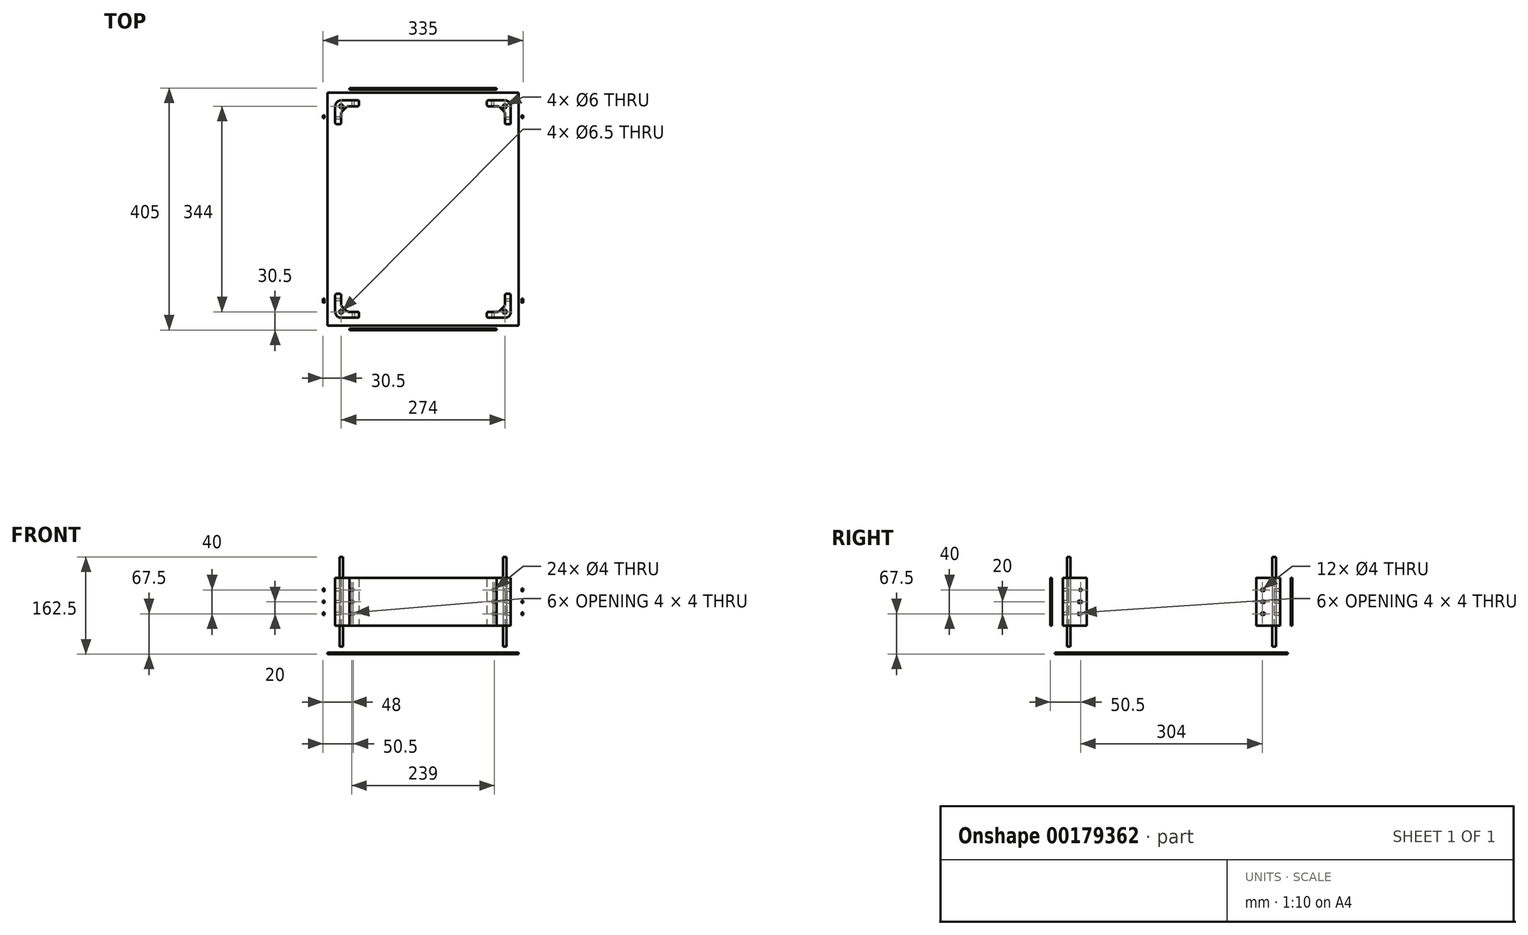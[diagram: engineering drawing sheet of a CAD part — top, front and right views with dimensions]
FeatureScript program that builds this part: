
annotation { "Feature Type Name" : "Feature", "Feature Type Description" : "" }
export const myFeature = defineFeature(function(context is Context, id is Id, definition is map)
    precondition{}
    {
        {
            var Q0;
            Q0=qCreatedBy(makeId("Top.planeOp"),FACE);
            var sketch = newSketch(context, id + "F0", { "sketchPlane" : qUnion([Q0])});
            skLineSegment(sketch, "E0.bottom", {"start": v(140, -175) * mm, "end": v(-140, -175) * mm, "construction": true});
            skLineSegment(sketch, "E0.top", {"start": v(140, 175) * mm, "end": v(-140, 175) * mm, "construction": true});
            skLineSegment(sketch, "E0.left", {"start": v(140, -175) * mm, "end": v(140, 175) * mm, "construction": true});
            skLineSegment(sketch, "E0.right", {"start": v(-140, -175) * mm, "end": v(-140, 175) * mm, "construction": true});
            skLineSegment(sketch, "E1", {"start": v(-134, 175) * mm, "end": v(-134, -175) * mm, "construction": true});
            skLineSegment(sketch, "E2", {"start": v(-140, -169) * mm, "end": v(140, -169) * mm, "construction": true});
            skLineSegment(sketch, "E3", {"start": v(134, -175) * mm, "end": v(134, 175) * mm, "construction": true});
            skLineSegment(sketch, "E4", {"start": v(-140, 169) * mm, "end": v(140, 169) * mm, "construction": true});
            skPoint(sketch, "E5", {"position": v(-134, -169) * mm});
            skPoint(sketch, "E6", {"position": v(134, -169) * mm});
            skPoint(sketch, "E7", {"position": v(134, 169) * mm});
            skPoint(sketch, "E8", {"position": v(-134, 169) * mm});
            skLineSegment(sketch, "E9", {"start": v(-140, 175) * mm, "end": v(-134, 169) * mm, "construction": true});
            skLineSegment(sketch, "E10", {"start": v(-134, 175) * mm, "end": v(-140, 169) * mm, "construction": true});
            skPoint(sketch, "E11", {"position": v(-137, 172) * mm});
            skCircle(sketch, "E12", {"center": v(-137, 172) * mm, "radius": 3 * mm});
            skLineSegment(sketch, "E13", {"start": v(134, 169) * mm, "end": v(140, 175) * mm, "construction": true});
            skLineSegment(sketch, "E14", {"start": v(134, 175) * mm, "end": v(140, 169) * mm, "construction": true});
            skPoint(sketch, "E15", {"position": v(137, 172) * mm});
            skCircle(sketch, "E16", {"center": v(137, 172) * mm, "radius": 3 * mm});
            skLineSegment(sketch, "E17", {"start": v(134, -169) * mm, "end": v(140, -175) * mm, "construction": true});
            skLineSegment(sketch, "E18", {"start": v(140, -169) * mm, "end": v(134, -175) * mm, "construction": true});
            skPoint(sketch, "E19", {"position": v(137, -172) * mm});
            skCircle(sketch, "E20", {"center": v(137, -172) * mm, "radius": 3 * mm});
            skLineSegment(sketch, "E21", {"start": v(-134, -169) * mm, "end": v(-140, -175) * mm, "construction": true});
            skLineSegment(sketch, "E22", {"start": v(-140, -169) * mm, "end": v(-134, -175) * mm, "construction": true});
            skPoint(sketch, "E23", {"position": v(-137, -172) * mm});
            skCircle(sketch, "E24", {"center": v(-137, -172) * mm, "radius": 3 * mm});
            skLineSegment(sketch, "E25.bottom", {"start": v(160, -195) * mm, "end": v(-160, -195) * mm});
            skLineSegment(sketch, "E25.top", {"start": v(160, 195) * mm, "end": v(-160, 195) * mm});
            skLineSegment(sketch, "E25.left", {"start": v(160, -195) * mm, "end": v(160, 195) * mm});
            skLineSegment(sketch, "E25.right", {"start": v(-160, -195) * mm, "end": v(-160, 195) * mm});
            skPoint(sketch, "E25.middle", {"position": v(0, 0) * mm});
            skSolve(sketch);
        }
        {
            var Q0;
            Q0 = qSketchRegion(id + "F0", true);
            extrude(context, id + "F1", {"entities" : qUnion([Q0]), "depth" : 2.5 * mm});
        }
        {
            var Q0;
            Q0=makeQuery(id+"F1.opExtrude","CAP_FACE",FACE,{"disambiguationData":[OSD([sQuery(id+"F0.wireOp",EDGE,"E12"),sQuery(id+"F0.wireOp",EDGE,"E16"),sQuery(id+"F0.wireOp",EDGE,"E20"),sQuery(id+"F0.wireOp",EDGE,"E24"),sQuery(id+"F0.wireOp",EDGE,"E25.bottom"),sQuery(id+"F0.wireOp",EDGE,"E25.top"),sQuery(id+"F0.wireOp",EDGE,"E25.left"),sQuery(id+"F0.wireOp",EDGE,"E25.right")])],"isStart":false});
            cPlane(context, id + "F2", {"entities" : qUnion([Q0]), "cplaneType" : CPlaneType.OFFSET, "offset" : 10 * mm, "width" : 150 * mm, "height" : 150 * mm});
        }
        {
            var Q0;
            Q0=qCreatedBy(id+"F2.planeOp",FACE);
            var sketch = newSketch(context, id + "F3", { "sketchPlane" : qUnion([Q0])});
            skCircle(sketch, "E26", {"center": v(-137, -172) * mm, "radius": 3 * mm});
            skSolve(sketch);
        }
        {
            var Q0;
            Q0 = qSketchRegion(id + "F3", true);
            extrude(context, id + "F4", {"entities" : qUnion([Q0]), "depth" : 150 * mm});
        }
        {
            var Q0;
            Q0=makeQuery(id+"F4.opExtrude","SWEPT_BODY",BODY,{"disambiguationData":[OSD([sQuery(id+"F3.wireOp",EDGE,"E26")])]});
            var Q1;
            Q1=qCreatedBy(makeId("Right.planeOp"),FACE);
            mirror(context, id + "F5", {"entities" : qUnion([Q0]), "mirrorPlane" : qUnion([Q1])});
        }
        {
            var Q0;
            Q0=makeQuery(id+"F4.opExtrude","SWEPT_BODY",BODY,{"disambiguationData":[OSD([sQuery(id+"F3.wireOp",EDGE,"E26")])]});
            var Q1;
            Q1=makeQuery(id+"F5.opPattern","COPY",BODY,{"derivedFrom":makeQuery(id+"F4.opExtrude","SWEPT_BODY",BODY,{"disambiguationData":[OSD([sQuery(id+"F3.wireOp",EDGE,"E26")])]}),"instanceName":"1"});
            var Q2;
            Q2=qCreatedBy(makeId("Front.planeOp"),FACE);
            mirror(context, id + "F6", {"entities" : qUnion([Q0, Q1]), "mirrorPlane" : qUnion([Q2])});
        }
        {
            var Q0;
            Q0=qCreatedBy(id+"F2.planeOp",FACE);
            cPlane(context, id + "F7", {"entities" : qUnion([Q0]), "cplaneType" : CPlaneType.OFFSET, "offset" : 35 * mm, "width" : 150 * mm, "height" : 150 * mm});
        }
        {
            var Q0;
            Q0=qCreatedBy(id+"F7.planeOp",FACE);
            var sketch = newSketch(context, id + "F8", { "sketchPlane" : qUnion([Q0])});
            skCircle(sketch, "E27", {"center": v(-137, -172) * mm, "radius": 3.25 * mm});
            skLineSegment(sketch, "E28.bottom", {"start": v(-127, -182) * mm, "end": v(-147, -182) * mm, "construction": true});
            skLineSegment(sketch, "E28.top", {"start": v(-127, -162) * mm, "end": v(-147, -162) * mm, "construction": true});
            skLineSegment(sketch, "E28.left", {"start": v(-127, -182) * mm, "end": v(-127, -162) * mm, "construction": true});
            skLineSegment(sketch, "E28.right", {"start": v(-147, -182) * mm, "end": v(-147, -162) * mm, "construction": true});
            skLineSegment(sketch, "E29.bottom", {"start": v(-147, -162) * mm, "end": v(-127, -162) * mm, "construction": true});
            skLineSegment(sketch, "E29.top", {"start": v(-147, -142) * mm, "end": v(-127, -142) * mm, "construction": true});
            skLineSegment(sketch, "E29.left", {"start": v(-147, -162) * mm, "end": v(-147, -142) * mm, "construction": true});
            skLineSegment(sketch, "E29.right", {"start": v(-127, -162) * mm, "end": v(-127, -142) * mm, "construction": true});
            skLineSegment(sketch, "E30.bottom", {"start": v(-127, -162) * mm, "end": v(-107, -162) * mm, "construction": true});
            skLineSegment(sketch, "E30.top", {"start": v(-127, -182) * mm, "end": v(-107, -182) * mm, "construction": true});
            skLineSegment(sketch, "E30.left", {"start": v(-127, -162) * mm, "end": v(-127, -182) * mm, "construction": true});
            skLineSegment(sketch, "E30.right", {"start": v(-107, -162) * mm, "end": v(-107, -182) * mm, "construction": true});
            skLineSegment(sketch, "E31", {"start": v(-147, -142) * mm, "end": v(-147, -182) * mm});
            skLineSegment(sketch, "E32", {"start": v(-147, -182) * mm, "end": v(-107, -182) * mm});
            skLineSegment(sketch, "E33", {"start": v(-137, -142) * mm, "end": v(-137, -162) * mm, "construction": true});
            skLineSegment(sketch, "E34", {"start": v(-137, -162) * mm, "end": v(-137, -172) * mm, "construction": true});
            skLineSegment(sketch, "E35", {"start": v(-137, -172) * mm, "end": v(-127, -172) * mm, "construction": true});
            skLineSegment(sketch, "E36", {"start": v(-127, -172) * mm, "end": v(-107, -172) * mm, "construction": true});
            skLineSegment(sketch, "E37", {"start": v(-147, -142) * mm, "end": v(-137, -142) * mm});
            skLineSegment(sketch, "E38", {"start": v(-137, -142) * mm, "end": v(-137, -162) * mm});
            skLineSegment(sketch, "E39", {"start": v(-137, -162) * mm, "end": v(-127, -172) * mm});
            skLineSegment(sketch, "E40", {"start": v(-127, -172) * mm, "end": v(-107, -172) * mm});
            skLineSegment(sketch, "E41", {"start": v(-107, -172) * mm, "end": v(-107, -182) * mm});
            skSolve(sketch);
        }
        {
            var Q0;
            Q0=makeQuery(id+"F8.imprint","IMPRINT",FACE,{"disambiguationData":[TD([[makeQuery(id+"F8.imprint","IMPRINT",EDGE,{"derivedFrom":sQuery(id+"F8.wireOp",EDGE,"E27")}),-1.0]])]});
            extrude(context, id + "F9", {"entities" : qUnion([Q0]), "depth" : 80 * mm});
        }
        {
            var Q0;
            Q0=makeQuery(id+"F9.opExtrude","SWEPT_FACE",FACE,{"disambiguationData":[OSD([sQuery(id+"F8.wireOp",EDGE,"E32")])]});
            var sketch = newSketch(context, id + "F10", { "sketchPlane" : qUnion([Q0])});
            skLineSegment(sketch, "E42.bottom", {"start": v(-107, 127.5) * mm, "end": v(-127, 127.5) * mm, "construction": true});
            skLineSegment(sketch, "E42.top", {"start": v(-107, 47.5) * mm, "end": v(-127, 47.5) * mm, "construction": true});
            skLineSegment(sketch, "E42.left", {"start": v(-107, 127.5) * mm, "end": v(-107, 47.5) * mm, "construction": true});
            skLineSegment(sketch, "E42.right", {"start": v(-127, 127.5) * mm, "end": v(-127, 47.5) * mm, "construction": true});
            skLineSegment(sketch, "E43", {"start": v(-117, 127.5) * mm, "end": v(-117, 47.5) * mm, "construction": true});
            skCircle(sketch, "E44", {"center": v(-117, 87.5) * mm, "radius": 2 * mm});
            skCircle(sketch, "E45", {"center": v(-117, 107.5) * mm, "radius": 2 * mm});
            skCircle(sketch, "E46", {"center": v(-117, 67.5) * mm, "radius": 2 * mm});
            skSolve(sketch);
        }
        {
            var Q0;
            Q0=makeQuery(id+"F10.imprint","IMPRINT",FACE,{"disambiguationData":[TD([[makeQuery(id+"F10.imprint","IMPRINT",EDGE,{"derivedFrom":sQuery(id+"F10.wireOp",EDGE,"E45")}),1.0]])]});
            var Q1;
            Q1=makeQuery(id+"F10.imprint","IMPRINT",FACE,{"disambiguationData":[TD([[makeQuery(id+"F10.imprint","IMPRINT",EDGE,{"derivedFrom":sQuery(id+"F10.wireOp",EDGE,"E44")}),1.0]])]});
            var Q2;
            Q2=makeQuery(id+"F10.imprint","IMPRINT",FACE,{"disambiguationData":[TD([[makeQuery(id+"F10.imprint","IMPRINT",EDGE,{"derivedFrom":sQuery(id+"F10.wireOp",EDGE,"E46")}),1.0]])]});
            extrude(context, id + "F11", {"entities" : qUnion([Q0, Q1, Q2]), "operationType" : NewBodyOperationType.REMOVE, "endBound" : BoundingType.THROUGH_ALL, "oppositeDirection" : true, "depth" : 25 * mm});
        }
        {
            var Q0;
            Q0=makeQuery(id+"F9.opExtrude","SWEPT_FACE",FACE,{"disambiguationData":[OSD([sQuery(id+"F8.wireOp",EDGE,"E31")])]});
            var sketch = newSketch(context, id + "F12", { "sketchPlane" : qUnion([Q0])});
            skLineSegment(sketch, "E47.bottom", {"start": v(142, 127.5) * mm, "end": v(162, 127.5) * mm, "construction": true});
            skLineSegment(sketch, "E47.top", {"start": v(142, 47.5) * mm, "end": v(162, 47.5) * mm, "construction": true});
            skLineSegment(sketch, "E47.left", {"start": v(142, 127.5) * mm, "end": v(142, 47.5) * mm, "construction": true});
            skLineSegment(sketch, "E47.right", {"start": v(162, 127.5) * mm, "end": v(162, 47.5) * mm, "construction": true});
            skLineSegment(sketch, "E48", {"start": v(152, 127.5) * mm, "end": v(152, 47.5) * mm, "construction": true});
            skCircle(sketch, "E49", {"center": v(152, 87.5) * mm, "radius": 2 * mm});
            skCircle(sketch, "E50", {"center": v(152, 107.5) * mm, "radius": 2 * mm});
            skCircle(sketch, "E51", {"center": v(152, 67.5) * mm, "radius": 2 * mm});
            skSolve(sketch);
        }
        {
            var Q0;
            Q0 = qSketchRegion(id + "F12", true);
            extrude(context, id + "F13", {"entities" : qUnion([Q0]), "operationType" : NewBodyOperationType.REMOVE, "endBound" : BoundingType.THROUGH_ALL, "oppositeDirection" : true, "depth" : 25 * mm});
        }
        {
            var Q0;
            Q0=makeQuery(id+"F9.opExtrude","SWEPT_EDGE",EDGE,{"disambiguationData":[OSD([sQuery(id+"F8.wireOp",EDGE,"E31"),sQuery(id+"F8.wireOp",EDGE,"E32")])]});
            fillet(context, id + "F14", {"entities" : qUnion([Q0]), "radius" : 10 * mm, "tangentPropagation" : true, "allowEdgeOverflow" : false});
        }
        {
            var Q0;
            Q0=makeQuery(id+"F9.opExtrude","SWEPT_EDGE",EDGE,{"disambiguationData":[OSD([sQuery(id+"F8.wireOp",EDGE,"E32"),sQuery(id+"F8.wireOp",EDGE,"z4GfYlZF-26rS-DNWD-Nt1O-hA1oHAJZCPCR")])]});
            var Q1;
            Q1=makeQuery(id+"F9.opExtrude","SWEPT_EDGE",EDGE,{"disambiguationData":[OSD([sQuery(id+"F8.wireOp",EDGE,"E31"),sQuery(id+"F8.wireOp",EDGE,"z4GfYlZF-26rS-DNWD-Nt1O-hA1oHAJZCPCR")])]});
            var Q2;
            Q2=makeQuery(id+"F9.opExtrude","SWEPT_EDGE",EDGE,{"disambiguationData":[OSD([sQuery(id+"F8.wireOp",EDGE,"E40"),sQuery(id+"F8.wireOp",EDGE,"E41")])]});
            var Q3;
            Q3=makeQuery(id+"F9.opExtrude","SWEPT_EDGE",EDGE,{"disambiguationData":[OSD([sQuery(id+"F8.wireOp",EDGE,"E37"),sQuery(id+"F8.wireOp",EDGE,"E38")])]});
            fillet(context, id + "F15", {"entities" : qUnion([Q0, Q1, Q2, Q3]), "radius" : 2.5 * mm, "tangentPropagation" : true, "allowEdgeOverflow" : false});
        }
        {
            var Q0;
            Q0=makeQuery(id+"F9.opExtrude","SWEPT_EDGE",EDGE,{"disambiguationData":[OSD([sQuery(id+"F8.wireOp",EDGE,"E38"),sQuery(id+"F8.wireOp",EDGE,"E39")])]});
            var Q1;
            Q1=makeQuery(id+"F9.opExtrude","SWEPT_EDGE",EDGE,{"disambiguationData":[OSD([sQuery(id+"F8.wireOp",EDGE,"E39"),sQuery(id+"F8.wireOp",EDGE,"E40")])]});
            fillet(context, id + "F16", {"entities" : qUnion([Q0, Q1]), "radius" : 5 * mm, "tangentPropagation" : true, "allowEdgeOverflow" : false});
        }
        {
            var Q0;
            Q0=makeQuery(id+"F9.opExtrude","SWEPT_BODY",BODY,{"disambiguationData":[OSD([sQuery(id+"F8.wireOp",EDGE,"E27"),sQuery(id+"F8.wireOp",EDGE,"E31"),sQuery(id+"F8.wireOp",EDGE,"E32"),sQuery(id+"F8.wireOp",EDGE,"z4GfYlZF-26rS-DNWD-Nt1O-hA1oHAJZCPCR")])]});
            var Q1;
            Q1=qCreatedBy(makeId("Right.planeOp"),FACE);
            mirror(context, id + "F17", {"entities" : qUnion([Q0]), "mirrorPlane" : qUnion([Q1])});
        }
        {
            var Q0;
            Q0=makeQuery(id+"F9.opExtrude","SWEPT_BODY",BODY,{"disambiguationData":[OSD([sQuery(id+"F8.wireOp",EDGE,"E27"),sQuery(id+"F8.wireOp",EDGE,"E31"),sQuery(id+"F8.wireOp",EDGE,"E32"),sQuery(id+"F8.wireOp",EDGE,"z4GfYlZF-26rS-DNWD-Nt1O-hA1oHAJZCPCR")])]});
            var Q1;
            Q1=makeQuery(id+"F17.opPattern","COPY",BODY,{"derivedFrom":makeQuery(id+"F9.opExtrude","SWEPT_BODY",BODY,{"disambiguationData":[OSD([sQuery(id+"F8.wireOp",EDGE,"E27"),sQuery(id+"F8.wireOp",EDGE,"E31"),sQuery(id+"F8.wireOp",EDGE,"E32"),sQuery(id+"F8.wireOp",EDGE,"z4GfYlZF-26rS-DNWD-Nt1O-hA1oHAJZCPCR")])]}),"instanceName":"1"});
            var Q2;
            Q2=qCreatedBy(makeId("Front.planeOp"),FACE);
            mirror(context, id + "F18", {"entities" : qUnion([Q0, Q1]), "mirrorPlane" : qUnion([Q2])});
        }
        {
            var Q0;
            Q0=qCreatedBy(makeId("Front.planeOp"),FACE);
            cPlane(context, id + "F19", {"entities" : qUnion([Q0]), "cplaneType" : CPlaneType.OFFSET, "offset" : 200 * mm, "width" : 150 * mm, "height" : 150 * mm});
        }
        {
            var Q0;
            Q0=qCreatedBy(id+"F19.planeOp",FACE);
            var sketch = newSketch(context, id + "F20", { "sketchPlane" : qUnion([Q0])});
            skLineSegment(sketch, "E52.bottom", {"start": v(-123.25, 127.5) * mm, "end": v(123.25, 127.5) * mm});
            skLineSegment(sketch, "E52.top", {"start": v(-123.25, 47.5) * mm, "end": v(123.25, 47.5) * mm});
            skLineSegment(sketch, "E52.left", {"start": v(-123.25, 127.5) * mm, "end": v(-123.25, 47.5) * mm});
            skLineSegment(sketch, "E52.right", {"start": v(123.25, 127.5) * mm, "end": v(123.25, 47.5) * mm});
            skCircle(sketch, "E53", {"center": v(-119.5, 107.5) * mm, "radius": 2 * mm});
            skCircle(sketch, "E54", {"center": v(-119.5, 87.5) * mm, "radius": 2 * mm});
            skCircle(sketch, "E55", {"center": v(-119.5, 67.5) * mm, "radius": 2 * mm});
            skCircle(sketch, "E56", {"center": v(119.5, 107.5) * mm, "radius": 2 * mm});
            skCircle(sketch, "E57", {"center": v(119.5, 87.5) * mm, "radius": 2 * mm});
            skCircle(sketch, "E58", {"center": v(119.5, 67.5) * mm, "radius": 2 * mm});
            skSolve(sketch);
        }
        {
            var Q0;
            Q0 = qSketchRegion(id + "F20", true);
            extrude(context, id + "F21", {"entities" : qUnion([Q0]), "depth" : 2.5 * mm});
        }
        {
            var Q0;
            Q0=makeQuery(id+"F21.opExtrude","SWEPT_BODY",BODY,{"disambiguationData":[OSD([sQuery(id+"F20.wireOp",EDGE,"E52.bottom"),sQuery(id+"F20.wireOp",EDGE,"E52.top"),sQuery(id+"F20.wireOp",EDGE,"E52.left"),sQuery(id+"F20.wireOp",EDGE,"E52.right"),sQuery(id+"F20.wireOp",EDGE,"E53"),sQuery(id+"F20.wireOp",EDGE,"E54"),sQuery(id+"F20.wireOp",EDGE,"E55"),sQuery(id+"F20.wireOp",EDGE,"E56"),sQuery(id+"F20.wireOp",EDGE,"E57"),sQuery(id+"F20.wireOp",EDGE,"E58")])]});
            var Q1;
            Q1=qCreatedBy(makeId("Front.planeOp"),FACE);
            mirror(context, id + "F22", {"entities" : qUnion([Q0]), "mirrorPlane" : qUnion([Q1])});
        }
        {
            var Q0;
            Q0=qCreatedBy(makeId("Right.planeOp"),FACE);
            cPlane(context, id + "F23", {"entities" : qUnion([Q0]), "cplaneType" : CPlaneType.OFFSET, "offset" : 165 * mm, "width" : 150 * mm, "height" : 150 * mm});
        }
        {
            var Q0;
            Q0=qCreatedBy(id+"F23.planeOp",FACE);
            var sketch = newSketch(context, id + "F24", { "sketchPlane" : qUnion([Q0])});
            skLineSegment(sketch, "E59.bottom", {"start": v(-158.25, 127.5) * mm, "end": v(158.25, 127.5) * mm});
            skLineSegment(sketch, "E59.top", {"start": v(-158.25, 47.5) * mm, "end": v(158.25, 47.5) * mm});
            skLineSegment(sketch, "E59.right", {"start": v(158.25, 127.5) * mm, "end": v(158.25, 47.5) * mm});
            skCircle(sketch, "E60", {"center": v(-152, 107.5) * mm, "radius": 2 * mm});
            skCircle(sketch, "E61", {"center": v(-154.5, 87.5) * mm, "radius": 2 * mm});
            skCircle(sketch, "E62", {"center": v(-154.5, 67.5) * mm, "radius": 2 * mm});
            skCircle(sketch, "E63", {"center": v(154.5, 107.5) * mm, "radius": 2 * mm});
            skCircle(sketch, "E64", {"center": v(154.5, 87.5) * mm, "radius": 2 * mm});
            skCircle(sketch, "E65", {"center": v(154.5, 67.5) * mm, "radius": 2 * mm});
            skSolve(sketch);
        }
        {
            var Q0;
            Q0 = qSketchRegion(id + "F24", true);
            extrude(context, id + "F25", {"entities" : qUnion([Q0]), "depth" : 2.5 * mm});
        }
        {
            var Q0;
            Q0=makeQuery(id+"F25.opExtrude","SWEPT_BODY",BODY,{"disambiguationData":[OSD([sQuery(id+"F24.wireOp",EDGE,"E59.bottom"),sQuery(id+"F24.wireOp",EDGE,"E59.top"),sQuery(id+"F24.wireOp",EDGE,"E59.left"),sQuery(id+"F24.wireOp",EDGE,"E59.right"),sQuery(id+"F24.wireOp",EDGE,"E60"),sQuery(id+"F24.wireOp",EDGE,"E61"),sQuery(id+"F24.wireOp",EDGE,"E62"),sQuery(id+"F24.wireOp",EDGE,"E63"),sQuery(id+"F24.wireOp",EDGE,"E64"),sQuery(id+"F24.wireOp",EDGE,"E65")])]});
            var Q1;
            Q1=qCreatedBy(makeId("Right.planeOp"),FACE);
            mirror(context, id + "F26", {"entities" : qUnion([Q0]), "mirrorPlane" : qUnion([Q1])});
        }
    });
